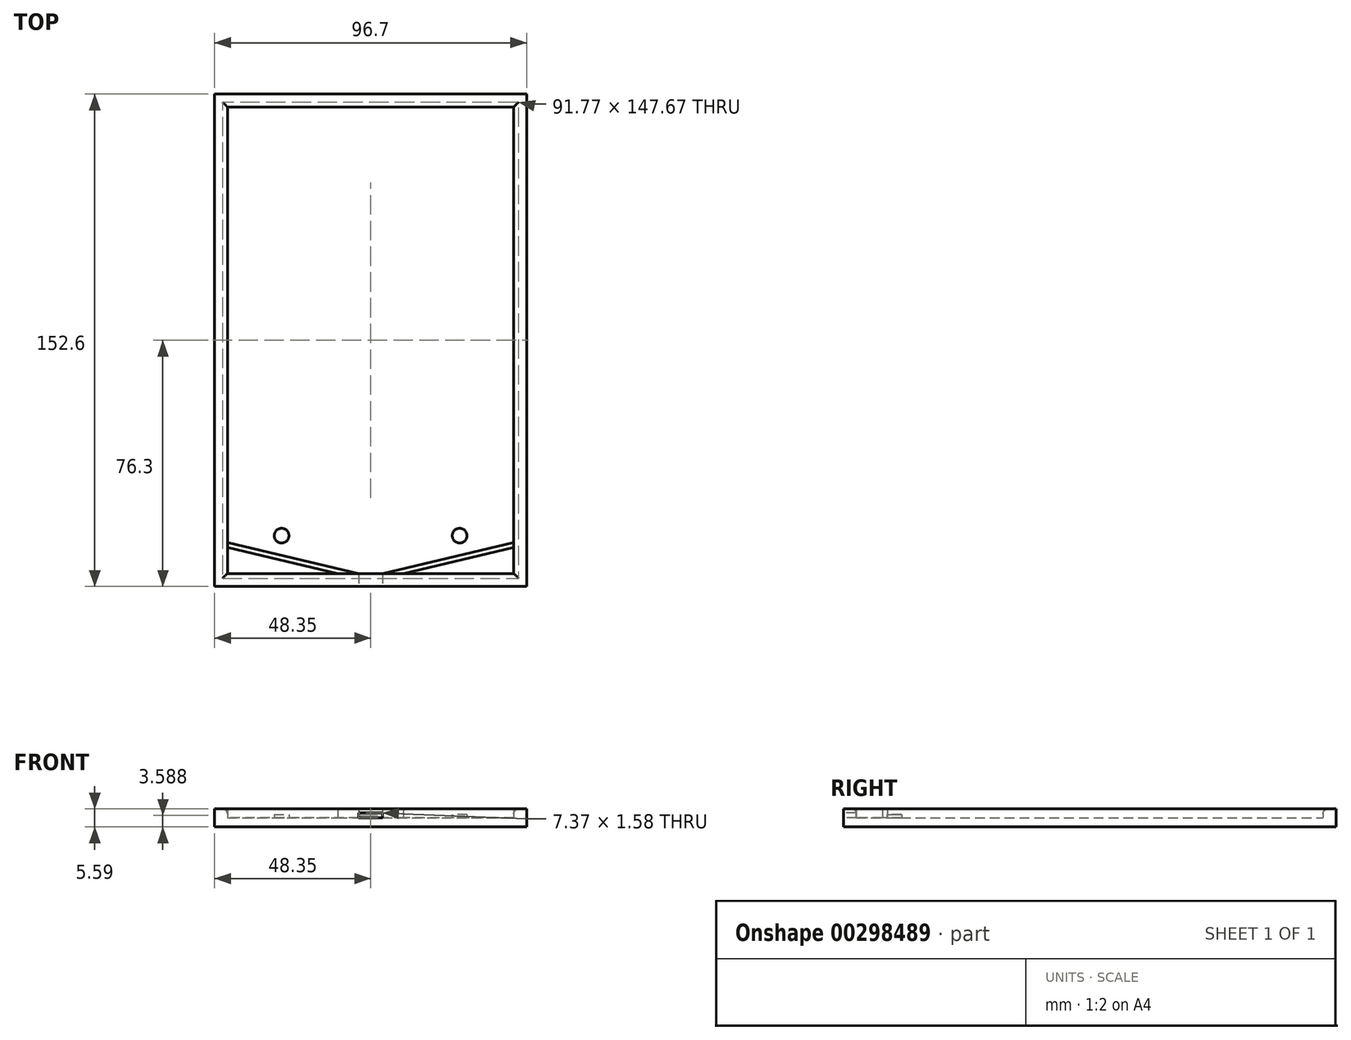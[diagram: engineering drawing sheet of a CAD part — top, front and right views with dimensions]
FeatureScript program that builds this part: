
annotation { "Feature Type Name" : "Feature", "Feature Type Description" : "" }
export const myFeature = defineFeature(function(context is Context, id is Id, definition is map)
    precondition{}
    {
        {
            var Q0;
            Q0=qCreatedBy(makeId("Top.planeOp"),FACE);
            var sketch = newSketch(context, id + "F0", { "sketchPlane" : qUnion([Q0])});
            skLineSegment(sketch, "E0.bottom", {"start": v(-48.35, 76.3) * mm, "end": v(48.35, 76.3) * mm});
            skLineSegment(sketch, "E0.top", {"start": v(-48.35, -76.3) * mm, "end": v(48.35, -76.3) * mm});
            skLineSegment(sketch, "E0.left", {"start": v(-48.35, 76.3) * mm, "end": v(-48.35, -76.3) * mm});
            skLineSegment(sketch, "E0.right", {"start": v(48.35, 76.3) * mm, "end": v(48.35, -76.3) * mm});
            skPoint(sketch, "E0.middle", {"position": v(0, 0) * mm});
            skSolve(sketch);
        }
        {
            var Q0;
            Q0 = qSketchRegion(id + "F0", true);
            extrude(context, id + "F1", {"entities" : qUnion([Q0]), "endBound" : BoundingType.SYMMETRIC, "depth" : 2.8 * mm});
        }
        {
            var Q0;
            Q0=makeQuery(id+"F1.opExtrude","CAP_FACE",FACE,{"disambiguationData":[OSD([sQuery(id+"F0.wireOp",EDGE,"E0.bottom"),sQuery(id+"F0.wireOp",EDGE,"E0.top"),sQuery(id+"F0.wireOp",EDGE,"E0.left"),sQuery(id+"F0.wireOp",EDGE,"E0.right")])],"isStart":false});
            var sketch = newSketch(context, id + "F2", { "sketchPlane" : qUnion([Q0])});
            skLineSegment(sketch, "E1", {"start": v(-48.35, 76.3) * mm, "end": v(48.35, 76.3) * mm});
            skLineSegment(sketch, "E2", {"start": v(48.35, 76.3) * mm, "end": v(48.35, -76.3) * mm});
            skLineSegment(sketch, "E3", {"start": v(48.35, -76.3) * mm, "end": v(-48.35, -76.3) * mm});
            skLineSegment(sketch, "E4", {"start": v(-48.35, -76.3) * mm, "end": v(-48.35, 76.3) * mm});
            skLineSegment(sketch, "E5", {"start": v(-44.36, -72.31) * mm, "end": v(-44.36, 72.31) * mm});
            skLineSegment(sketch, "E6", {"start": v(-44.36, 72.31) * mm, "end": v(44.36, 72.31) * mm});
            skLineSegment(sketch, "E7", {"start": v(44.36, 72.31) * mm, "end": v(44.36, -72.31) * mm});
            skLineSegment(sketch, "E8", {"start": v(44.36, -72.31) * mm, "end": v(-44.36, -72.31) * mm});
            skSolve(sketch);
        }
        {
            var Q0;
            Q0 = qSketchRegion(id + "F2", true);
            extrude(context, id + "F3", {"entities" : qUnion([Q0]), "operationType" : NewBodyOperationType.ADD, "depth" : 2.8 * mm});
        }
        {
            var Q0;
            Q0=makeQuery(id+"F3.opExtrude","CAP_EDGE",EDGE,{"disambiguationData":[OSD([sQuery(id+"F2.wireOp",EDGE,"E5")])],"isStart":false});
            var Q1;
            Q1=makeQuery(id+"F3.opExtrude","CAP_EDGE",EDGE,{"disambiguationData":[OSD([sQuery(id+"F2.wireOp",EDGE,"E6")])],"isStart":false});
            var Q2;
            Q2=makeQuery(id+"F3.opExtrude","CAP_EDGE",EDGE,{"disambiguationData":[OSD([sQuery(id+"F2.wireOp",EDGE,"E7")])],"isStart":false});
            var Q3;
            Q3=makeQuery(id+"F3.opExtrude","CAP_EDGE",EDGE,{"disambiguationData":[OSD([sQuery(id+"F2.wireOp",EDGE,"E8")])],"isStart":false});
            fillet(context, id + "F4", {"entities" : qUnion([Q0, Q1, Q2, Q3]), "radius" : 1.52 * mm, "tangentPropagation" : true, "allowEdgeOverflow" : false});
        }
        {
            var Q0;
            Q0=makeQuery(id+"F1.opExtrude","CAP_FACE",FACE,{"disambiguationData":[OSD([sQuery(id+"F0.wireOp",EDGE,"E0.bottom"),sQuery(id+"F0.wireOp",EDGE,"E0.top"),sQuery(id+"F0.wireOp",EDGE,"E0.left"),sQuery(id+"F0.wireOp",EDGE,"E0.right")])],"isStart":false});
            var sketch = newSketch(context, id + "F5", { "sketchPlane" : qUnion([Q0])});
            skCircle(sketch, "E9", {"center": v(27.59, -60.58) * mm, "radius": 2.29 * mm});
            skSolve(sketch);
        }
        {
            var Q0;
            Q0 = qSketchRegion(id + "F5", true);
            extrude(context, id + "F6", {"entities" : qUnion([Q0]), "operationType" : NewBodyOperationType.ADD, "depth" : 1.02 * mm});
        }
        {
            var Q0;
            Q0=makeQuery(id+"F1.opExtrude","SWEPT_BODY",BODY,{"disambiguationData":[OSD([sQuery(id+"F0.wireOp",EDGE,"E0.bottom"),sQuery(id+"F0.wireOp",EDGE,"E0.top"),sQuery(id+"F0.wireOp",EDGE,"E0.left"),sQuery(id+"F0.wireOp",EDGE,"E0.right")])]});
            var Q1;
            Q1=qCreatedBy(makeId("Right.planeOp"),FACE);
            mirror(context, id + "F7", {"entities" : qUnion([Q0]), "mirrorPlane" : qUnion([Q1])});
        }
        {
            var Q0;
            Q0=makeQuery(id+"F3.boolean.opBoolean","MERGE",FACE,{"derivedFrom":[makeQuery(id+"F1.opExtrude","SWEPT_FACE",FACE,{"disambiguationData":[OSD([sQuery(id+"F0.wireOp",EDGE,"E0.top")])]}),makeQuery(id+"F3.opExtrude","SWEPT_FACE",FACE,{"disambiguationData":[OSD([sQuery(id+"F2.wireOp",EDGE,"E3")])]})]});
            var sketch = newSketch(context, id + "F8", { "sketchPlane" : qUnion([Q0])});
            skLineSegment(sketch, "E10", {"start": v(-3.68, 1.4) * mm, "end": v(3.68, 1.4) * mm});
            skLineSegment(sketch, "E11", {"start": v(-3.68, 1.4) * mm, "end": v(-3.68, 2.98) * mm});
            skLineSegment(sketch, "E12", {"start": v(-3.68, 2.98) * mm, "end": v(3.68, 2.98) * mm});
            skLineSegment(sketch, "E13", {"start": v(3.68, 2.98) * mm, "end": v(3.68, 1.4) * mm});
            skSolve(sketch);
        }
        {
            var Q0;
            Q0 = qSketchRegion(id + "F8", true);
            extrude(context, id + "F9", {"entities" : qUnion([Q0]), "operationType" : NewBodyOperationType.REMOVE, "oppositeDirection" : true, "depth" : 25.4 * mm});
        }
        {
            var Q0;
            Q0=makeQuery(id+"F9.boolean.opBoolean","MERGE",FACE,{"derivedFrom":[makeQuery(id+"F1.opExtrude","CAP_FACE",FACE,{"disambiguationData":[OSD([sQuery(id+"F0.wireOp",EDGE,"E0.bottom"),sQuery(id+"F0.wireOp",EDGE,"E0.top"),sQuery(id+"F0.wireOp",EDGE,"E0.left"),sQuery(id+"F0.wireOp",EDGE,"E0.right")])],"isStart":false}),makeQuery(id+"F9.opExtrude","SWEPT_FACE",FACE,{"disambiguationData":[OSD([sQuery(id+"F8.wireOp",EDGE,"E10")])]})]});
            var sketch = newSketch(context, id + "F10", { "sketchPlane" : qUnion([Q0])});
            skLineSegment(sketch, "E14", {"start": v(3.68, -72.31) * mm, "end": v(44.36, -62.7) * mm});
            skLineSegment(sketch, "E15", {"start": v(44.36, -62.7) * mm, "end": v(44.36, -65.78) * mm});
            skLineSegment(sketch, "E16", {"start": v(44.36, -64.24) * mm, "end": v(10.2, -72.31) * mm});
            skLineSegment(sketch, "E17", {"start": v(10.2, -72.31) * mm, "end": v(3.68, -72.31) * mm});
            skSolve(sketch);
        }
        {
            var Q0;
            Q0 = qSketchRegion(id + "F10", true);
            extrude(context, id + "F11", {"entities" : qUnion([Q0]), "depth" : 2.8 * mm});
        }
        {
            var Q0;
            Q0=makeQuery(id+"F11.opExtrude","SWEPT_BODY",BODY,{"disambiguationData":[OSD([sQuery(id+"F10.wireOp",EDGE,"E14"),sQuery(id+"F10.wireOp",EDGE,"E15"),sQuery(id+"F10.wireOp",EDGE,"E16"),sQuery(id+"F10.wireOp",EDGE,"E17")])]});
            var Q1;
            Q1=qCreatedBy(makeId("Right.planeOp"),FACE);
            mirror(context, id + "F12", {"entities" : qUnion([Q0]), "mirrorPlane" : qUnion([Q1])});
        }
    });
